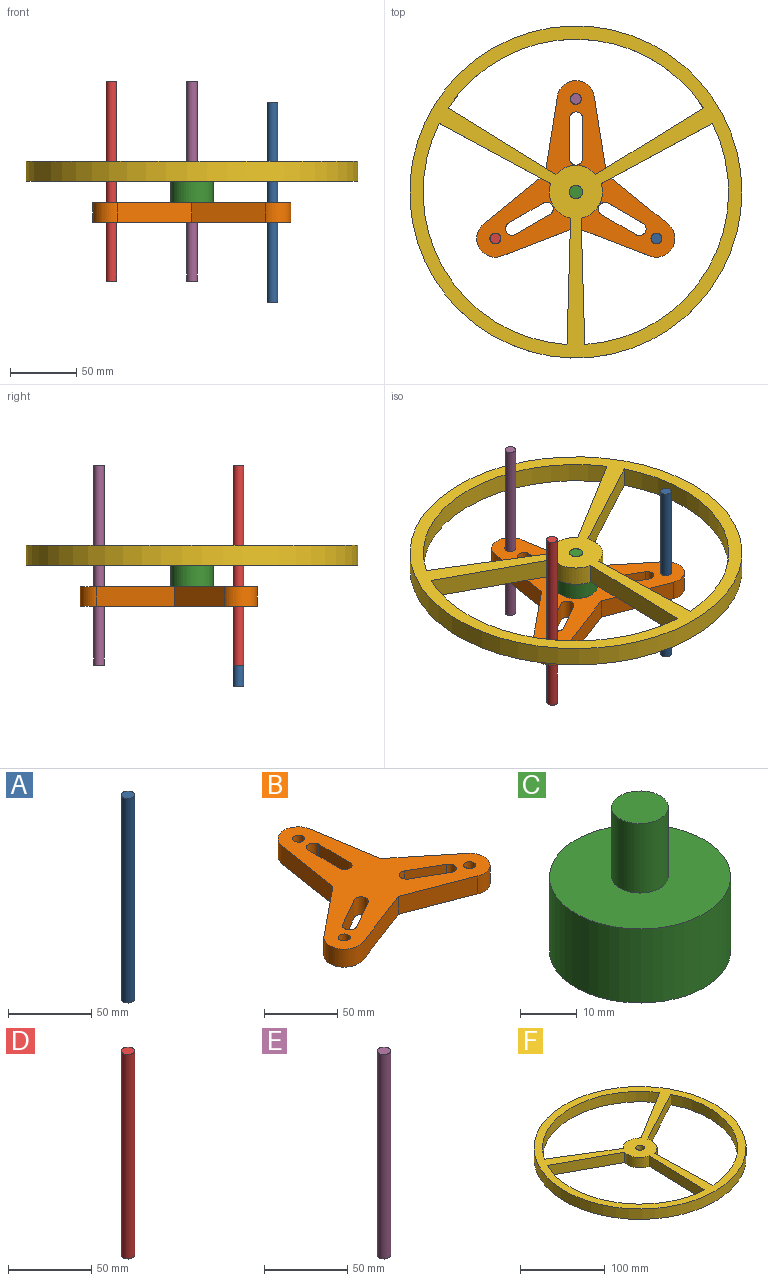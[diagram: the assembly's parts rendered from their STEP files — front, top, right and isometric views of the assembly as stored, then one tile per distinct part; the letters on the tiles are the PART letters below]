
ASSEMBLY  parts=6 mates=5
PART A: 3 faces, bbox 8x8x150 mm
  f0: cylinder r=4mm len=150mm, axis (0,0,-1), area 3769.9mm2, adj f1,f2
  f1: plane 8x8mm, normal (0,0,1), area 50.3mm2, adj f0
  f2: plane 8x8mm, normal (0,0,-1), area 50.3mm2, adj f0
PART B: 26 faces, bbox 149.2x133x15 mm
  f0: plane 25.98x15mm, normal (0.5,0.87,0), area 450mm2, adj f1,f18,f24,f25
  f1: cylinder r=5mm len=15mm, axis (0,0,-1), area 237.5mm2, adj f0,f2,f24,f25
  f2: plane 25.98x15mm, normal (-0.5,-0.87,0), area 450mm2, adj f1,f18,f24,f25
  f3: plane 25.98x15mm, normal (0.5,-0.87,0), area 450mm2, adj f4,f19,f24,f25
  f4: cylinder r=5mm len=15mm, axis (0,0,-1), area 237.5mm2, adj f3,f5,f24,f25
  f5: plane 25.98x15mm, normal (-0.5,0.87,0), area 450mm2, adj f4,f19,f24,f25
  f6: cylinder r=14mm len=27.65mm, axis (0,0,-1), area 593.5mm2, adj f7,f21,f24,f25
  f7: plane 58.81x15mm, normal (-0.99,0.16,0), area 893.3mm2, adj f6,f8,f24,f25
  f8: plane 46.26x37.51mm, normal (-0.63,0.78,0), area 893.3mm2, adj f7,f9,f24,f25
  f9: cylinder r=14mm len=24.87mm, axis (0,0,-1), area 593.5mm2, adj f8,f10,f24,f25
  f10: plane 55.61x21.3mm, normal (0.36,-0.93,0), area 893.3mm2, adj f9,f11,f24,f25
  f11: plane 55.61x21.3mm, normal (-0.36,-0.93,0), area 893.3mm2, adj f10,f12,f24,f25
  f12: cylinder r=14mm len=24.87mm, axis (0,0,-1), area 593.5mm2, adj f11,f13,f24,f25
  f13: plane 46.26x37.51mm, normal (0.63,0.78,0), area 893.3mm2, adj f12,f21,f24,f25
  f14: cylinder r=5mm len=15mm, axis (0,0,-1), area 233.8mm2, adj f15,f22,f24,f25
  f15: plane 30x15mm, normal (-1,0,0), area 450mm2, adj f14,f16,f24,f25
  f16: cylinder r=5mm len=15mm, axis (0,0,-1), area 237.5mm2, adj f15,f22,f24,f25
  f17: cylinder r=4.1mm len=15mm, axis (0,0,-1), area 386.4mm2, adj f24,f25
  f18: cylinder r=5mm len=15mm, axis (0,0,-1), area 233.8mm2, adj f0,f2,f24,f25
  f19: cylinder r=5mm len=15mm, axis (0,0,-1), area 233.8mm2, adj f3,f5,f24,f25
  f20: cylinder r=4.1mm len=15mm, axis (0,0,-1), area 386.4mm2, adj f24,f25
  f21: plane 58.81x15mm, normal (0.99,0.16,0), area 893.3mm2, adj f6,f13,f24,f25
  f22: plane 30x15mm, normal (1,0,0), area 450mm2, adj f14,f16,f24,f25
  f23: cylinder r=4.1mm len=15mm, axis (0,0,-1), area 386.4mm2, adj f24,f25
  f24: plane 149.24x133mm, normal (0,0,1), area 6906.8mm2, adj f0,f1,f2,f3,f4,f5,f6,f7
  f25: plane 149.24x133mm, normal (0,0,-1), area 6906.8mm2, adj f0,f1,f2,f3,f4,f5,f6,f7
PART C: 5 faces, bbox 32x32x31 mm
  f0: cylinder r=16mm len=32mm, axis (0,0,-1), area 1608.5mm2, adj f1,f2
  f1: plane 32x32mm, normal (0,0,1), area 725.7mm2, adj f0,f3
  f2: plane 32x32mm, normal (0,0,-1), area 804.2mm2, adj f0
  f3: cylinder r=5mm len=15mm, axis (0,0,-1), area 471.2mm2, adj f1,f4
  f4: plane 10x10mm, normal (0,0,1), area 78.5mm2, adj f3
PART D: 3 faces, bbox 8x8x150 mm
  f0: cylinder r=4mm len=150mm, axis (0,0,-1), area 3769.9mm2, adj f1,f2
  f1: plane 8x8mm, normal (0,0,1), area 50.3mm2, adj f0
  f2: plane 8x8mm, normal (0,0,-1), area 50.3mm2, adj f0
PART E: 3 faces, bbox 8x8x150 mm
  f0: cylinder r=4mm len=150mm, axis (0,0,-1), area 3769.9mm2, adj f1,f2
  f1: plane 8x8mm, normal (0,0,1), area 50.3mm2, adj f0
  f2: plane 8x8mm, normal (0,0,-1), area 50.3mm2, adj f0
PART F: 16 faces, bbox 250x250x15 mm
  f0: plane 95.2x15mm, normal (-1,0.03,0), area 1428.6mm2, adj f1,f9,f13,f14
  f1: cylinder r=115mm len=166.39mm, axis (0,0,-1), area 3412mm2, adj f0,f2,f13,f14
  f2: plane 83.82x45.22mm, normal (-0.47,-0.88,0), area 1428.6mm2, adj f1,f9,f13,f14
  f3: cylinder r=115mm len=166.43mm, axis (0,0,-1), area 3412mm2, adj f4,f10,f13,f14
  f4: plane 95.2x15mm, normal (1,0.03,0), area 1428.6mm2, adj f3,f5,f13,f14
  f5: cylinder r=20mm len=25.97mm, axis (0,0,-1), area 508.5mm2, adj f4,f10,f13,f14
  f6: cylinder r=115mm len=192.16mm, axis (0,0,-1), area 3412mm2, adj f7,f11,f13,f14
  f7: plane 81.07x49.98mm, normal (-0.52,0.85,0), area 1428.6mm2, adj f6,f8,f13,f14
  f8: cylinder r=20mm len=29.99mm, axis (0,0,-1), area 508.5mm2, adj f7,f11,f13,f14
  f9: cylinder r=20mm len=25.97mm, axis (0,0,-1), area 508.5mm2, adj f0,f2,f13,f14
  f10: plane 83.8x45.26mm, normal (0.48,-0.88,0), area 1428.6mm2, adj f3,f5,f13,f14
  f11: plane 81.1x49.94mm, normal (0.52,0.85,0), area 1428.6mm2, adj f6,f8,f13,f14
  f12: cylinder r=125mm len=250mm, axis (0,0,-1), area 11781mm2, adj f13,f14
  f13: plane 250x250mm, normal (0,0,1), area 11757.2mm2, adj f0,f1,f2,f3,f4,f5,f6,f7
  f14: plane 250x250mm, normal (0,0,-1), area 11757.2mm2, adj f0,f1,f2,f3,f4,f5,f6,f7
  f15: cylinder r=5.1mm len=15mm, axis (0,0,-1), area 480.7mm2, adj f13,f14
PLACE A t=(0.14,0.14,-75)mm
PLACE B t=(0.14,0.14,-14.93)mm fixed
PLACE C t=(0.14,0.14,-15.93)mm
PLACE D t=(0.14,0.14,-59)mm
PLACE E t=(0.14,0.14,-59)mm
PLACE F t=(0.14,0.14,-23.93)mm
MATE cylindrical D.f0 <-> B.f9  axis (0,0,-1) through (-60.48,-34.86,16)mm
MATE fastened C.f0 <-> B.f24  axis (0,0,-1) through (0.14,0.14,0.07)mm
MATE cylindrical E.f0 <-> B.f6  axis (0,0,-1) through (0.14,70.14,16)mm
MATE cylindrical A.f0 <-> B.f12  axis (0,0,-1) through (60.76,-34.86,0)mm
MATE revolute F.f1 <-> C.f0  axis (0,0,1) through (0.14,0.14,31.07)mm
